# Revit family: IS_Conca_BC761_BIM_GB
name_source: partatom
category: Plumbing Fixtures
revit_build: Autodesk Revit 2017 (Build: 20160225_1515(x64)
units: mm (PartAtom-declared; Revit-internal decimal feet)

## family parameters
Always vertical = No
Cut with Voids When Loaded = No
OmniClass Number = 23.45.55.17
OmniClass Title = Mixing Faucets
Part Type = Normal
Room Calculation Point = No
Round Connector Dimension = Use Diameter
Shared = No
Work Plane-Based = No

## types (4) — shared parameters
Accessories = https://www.idealspec.co.uk
AreaUnits = millimeters
AssetType = Fixed
BIMObjectName = IS_IdealStandard_ShowerManualWaterSupplySets_Conca_BC761
BIMobject category = Sanitary: Taps & Mixer
BarCode = 3800861085737
Brand = Ideal Standard
Brand url = http://www.idealstandard.co.uk
ConnectionType = Plumbing
CurrencyUnit = £
CurrentRevision = 1
Date of publishing = 22/09/2020
Edition number = 1
ExpectedLife = 30
FaucetFunction = UNSET
FaucetOperation = OTHER
FaucetType = OTHER
FlushRate = 0.00 m³
GTIN code = https://3800861085737
Help = https://www.idealspec.co.uk
IFC Classification = Sanitary Terminal
IfcExportAs = IfcValveType
IfcExportType = FAUCET
Installation instructions = https://www.idealspec.co.uk
InstallationInstructions = https://www.idealspec.co.uk
IsBuiltIn = No
IsHighPressure = No
IsSingleFlush = No
LinearUnits = millimeters
MaintenanceInformation = https://www.idealspec.co.uk
Manufacturer = Ideal Standard (UK) Ltd
Manufacturer name = Ideal Standard
ManufacturerURL = https://www.idealspec.co.uk
Material = Brass
Material main = Brass
NBS Reference Code = 45-35-70/335
NBS Reference Description = Shower mixers
Name = ShowerManualWaterSupplySets_Conca_BC761_IdealStandard
NettWeight = 2,42 KG
NominalDepth = 88 mm
NominalHeight = 112 mm
NominalLength = 88 mm
NominalWidth = 294 mm
Product Guid = e7fa7c38-5ddd-4f22-8d1d-3b338524aeb1
Product SKU = BC761
Product certification = https://www.idealspec.co.uk
Product data url = https://bimobject.com
Product family = Conca
Product group = SHOWER MIXERS
Product name = CONCA SHR MXR EXPSD BR GUNM
Product url = https://www.idealstandard.co.uk
ProductInformation = https://www.idealspec.co.uk
QR code = http://bimobject.com
Shape = Cylindrical
Size = 294 x 88 x 112 mm
Space = Internal
SpareParts = https://fastpart-spares.co.uk
Technical description = https://www.idealspec.co.uk
TestPressure = 10 Bar
UNSPSC Code = 301815
URL = https://www.idealspec.co.uk
Uniclass 1.4 Code = L725111
Uniclass 1.4 Description = Mixer taps
Uniclass 2.0 Code = Pr_40_30_96_78
Uniclass 2.0 Description = Shower Manual Water Supply Sets
Uniclass 2015 Code = Pr_40_20_87_78
Uniclass 2015 Name = Shower manual water supply sets
Uniclass2015Code = Pr_40_20_87_78
Uniclass2015Title = Shower manual water supply sets
Uniclass2015Version = v1.1
Uniformat II Code = Pr_40_30_96_78
Uniformat II Description = Shower Manual Water Supply Sets
Version = 1
VolumeUnits = Litres
WRASURL = https://www.wras.co.uk
WarrantyDescription = Manufacturers Warranty
WarrantyDurationParts = 5
WarrantyDurationUnit = year
WarrantyGuarantorParts = https://www.idealspec.co.uk
zero-valued in all types: FlushingRate, InletConnectionSize, MaterialThickness, OutletConnectionSize

## per-type parameters (varying)
| type | Color | Description | Features | Finish | MainColor | Model | ModelNumber | ModelReference |
| BC761AA - CONCA SHR MXR EXPSD CHR | Chrome | Conca Single Lever exposed shower mixer - | Single lever exposed shower mixer - | Chrome | Chrome | BC761AA | BC761AA | Single lever exposed shower mixer - |
| BC761A2 - CONCA SHR MXR EXPSD BR GOLD | Brushed gold | Conca Single Lever exposed shower mixer - Covered nuts fixation | Single lever exposed shower mixer - Covered nuts fixation | Brushed gold | Brushed gold | BC761A2 | BC761A2 | Single lever exposed shower mixer - Covered nuts fixation |
| BC761A5 - CONCA SHR MXR EXPSD MGN GREY | Brushed Gun metal | Conca Single Lever exposed shower mixer - Covered nuts fixation | Single lever exposed shower mixer - Covered nuts fixation | Brushed Gun metal | Brushed Gun metal | BC761A5 | BC761A5 | Single lever exposed shower mixer - Covered nuts fixation |
| BC761GN - CONCA SHR MXR EXPSD SILV STORM | Brushed nickel | Conca Single Lever exposed shower mixer - Covered nuts fixation | Single lever exposed shower mixer - Covered nuts fixation | Brushed nickel | Brushed nickel | BC761GN | BC761GN | Single lever exposed shower mixer - Covered nuts fixation |

## geometry (parser evidence)
native form markers: Sweep x2
no freeform markers — native parametric forms only
